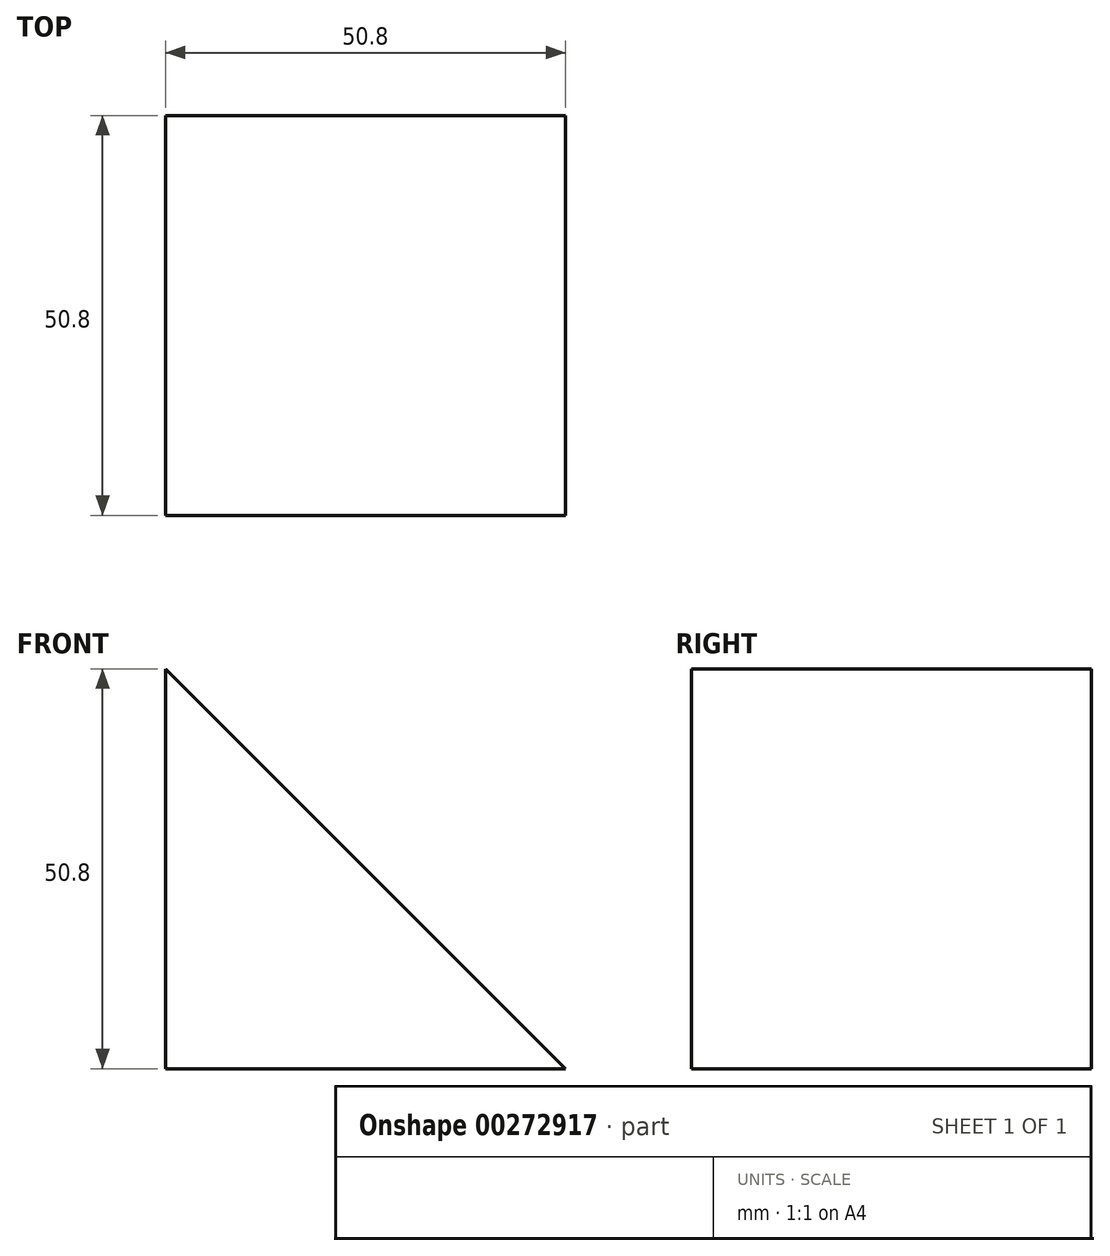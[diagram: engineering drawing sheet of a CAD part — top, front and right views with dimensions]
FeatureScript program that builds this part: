
annotation { "Feature Type Name" : "Feature", "Feature Type Description" : "" }
export const myFeature = defineFeature(function(context is Context, id is Id, definition is map)
    precondition{}
    {
        {
            var Q0;
            Q0=qCreatedBy(makeId("Front.planeOp"),FACE);
            var sketch = newSketch(context, id + "F0", { "sketchPlane" : qUnion([Q0])});
            skLineSegment(sketch, "E0", {"start": v(-63.59, 44.5) * mm, "end": v(-63.59, -6.3) * mm});
            skLineSegment(sketch, "E1", {"start": v(-63.59, -6.3) * mm, "end": v(-12.79, -6.3) * mm});
            skLineSegment(sketch, "E2", {"start": v(-63.59, 44.5) * mm, "end": v(-12.79, -6.3) * mm});
            skSolve(sketch);
        }
        {
            var Q0;
            Q0=makeQuery(id+"F0.imprint","IMPRINT",FACE,{"disambiguationData":[TD([[makeQuery(id+"F0.imprint","IMPRINT",EDGE,{"derivedFrom":sQuery(id+"F0.wireOp",EDGE,"E0")}),1.0]])]});
            extrude(context, id + "F1", {"entities" : qUnion([Q0]), "depth" : 50.8 * mm});
        }
    });
